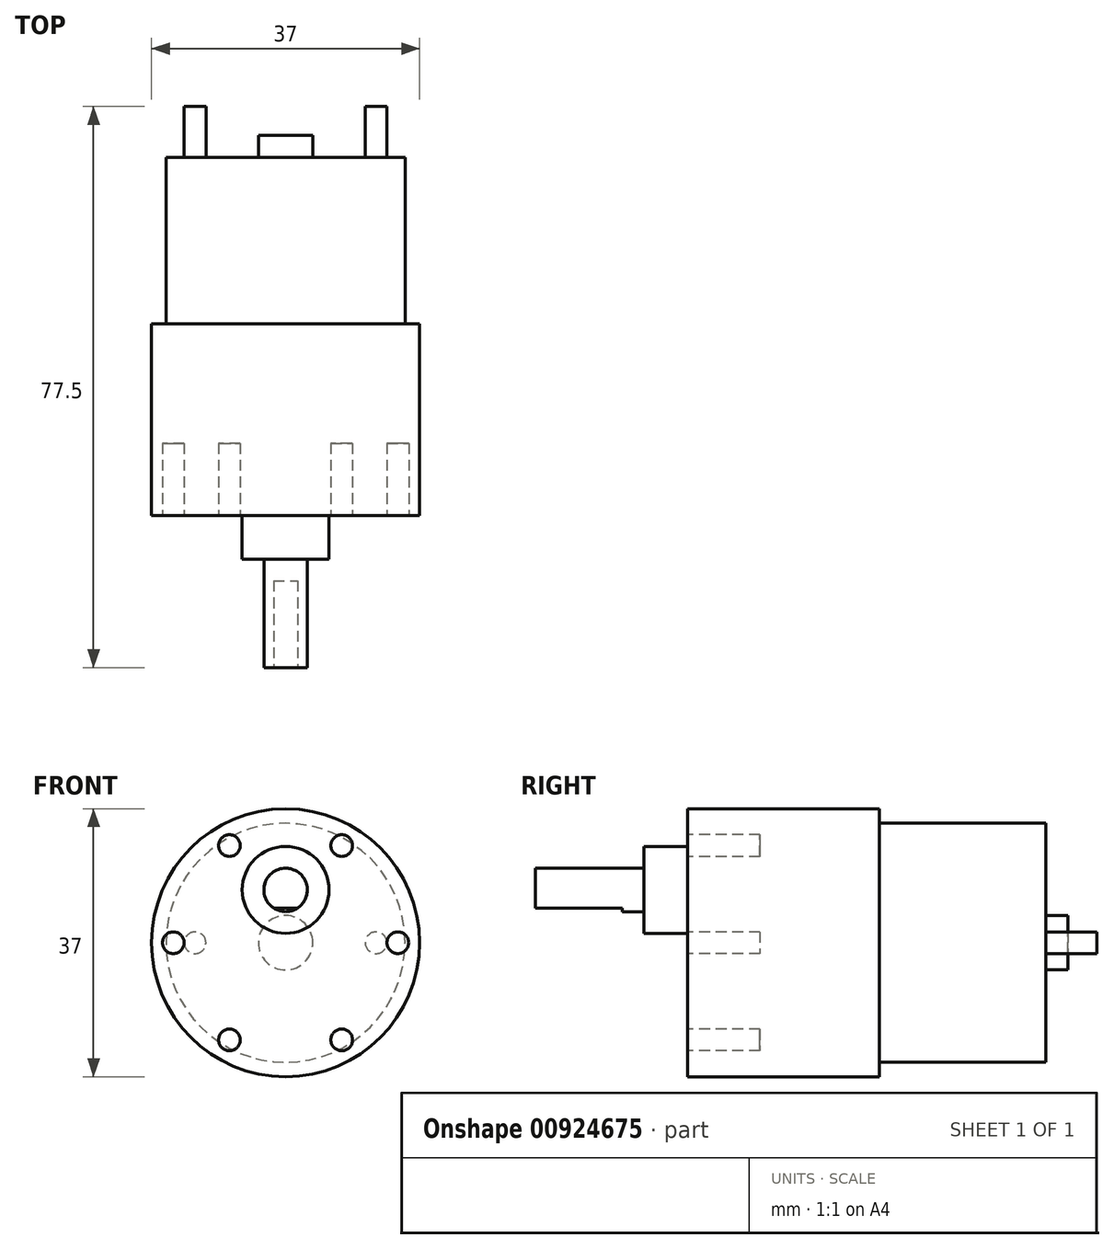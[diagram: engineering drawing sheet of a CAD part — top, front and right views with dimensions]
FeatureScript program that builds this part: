
annotation { "Feature Type Name" : "Feature", "Feature Type Description" : "" }
export const myFeature = defineFeature(function(context is Context, id is Id, definition is map)
    precondition{}
    {
        {
            var Q0;
            Q0=qCreatedBy(makeId("Front.planeOp"),FACE);
            var sketch = newSketch(context, id + "F0", { "sketchPlane" : qUnion([Q0])});
            skCircle(sketch, "E0", {"center": v(0, 0) * mm, "radius": 16.5 * mm});
            skCircle(sketch, "E1", {"center": v(0, 0) * mm, "radius": 18.5 * mm});
            skSolve(sketch);
        }
        {
            var Q0;
            Q0=qSketchRegion(id+"F0",true);
            var Q1;
            Q1=makeQuery(id+"F0.imprint","IMPRINT",FACE,{"disambiguationData":[TD([[makeQuery(id+"F0.imprint","IMPRINT",EDGE,{"derivedFrom":sQuery(id+"F0.wireOp",EDGE,"E0")}),1.0]])]});
            extrude(context, id + "F1", {"entities" : qUnion([Q0, Q1]), "depth" : 26.5 * mm, "offsetDistance" : 25 * mm});
        }
        {
            var Q0;
            Q0=makeQuery(id+"F0.imprint","IMPRINT",FACE,{"disambiguationData":[TD([[makeQuery(id+"F0.imprint","IMPRINT",EDGE,{"derivedFrom":sQuery(id+"F0.wireOp",EDGE,"E0")}),1.0]])]});
            extrude(context, id + "F2", {"entities" : qUnion([Q0]), "operationType" : NewBodyOperationType.ADD, "oppositeDirection" : true, "depth" : 23 * mm, "offsetDistance" : 25 * mm});
        }
        {
            var Q0;
            Q0=makeQuery(id+"F1.opExtrude","CAP_FACE",FACE,{"disambiguationData":[OSD([sQuery(id+"F0.wireOp",EDGE,"E1")])],"isStart":false});
            var sketch = newSketch(context, id + "F3", { "sketchPlane" : qUnion([Q0])});
            skCircle(sketch, "E2", {"center": v(0, 7.3) * mm, "radius": 6 * mm});
            skCircle(sketch, "E3", {"center": v(0, 7.3) * mm, "radius": 3 * mm});
            skPoint(sketch, "E4", {"position": v(0, 1.3) * mm});
            skCircle(sketch, "E5", {"center": v(-15.5, 0) * mm, "radius": 1.5 * mm});
            skSolve(sketch);
        }
        {
            var Q0;
            Q0=makeQuery(id+"F3.imprint","IMPRINT",FACE,{"disambiguationData":[TD([[makeQuery(id+"F3.imprint","IMPRINT",EDGE,{"derivedFrom":sQuery(id+"F3.wireOp",EDGE,"E2")}),1.0]])]});
            extrude(context, id + "F4", {"entities" : qUnion([Q0]), "operationType" : NewBodyOperationType.ADD, "depth" : 6 * mm, "offsetDistance" : 25 * mm});
        }
        {
            var Q0;
            Q0=makeQuery(id+"F4.boolean.opBoolean","SPLIT",FACE,{"disambiguationData":[TD([makeQuery(id+"F4.opExtrude","SWEPT_FACE",FACE,{"disambiguationData":[OSD([sQuery(id+"F3.wireOp",EDGE,"E3")])]})])],"derivedFrom":makeQuery(id+"F1.opExtrude","CAP_FACE",FACE,{"disambiguationData":[OSD([sQuery(id+"F0.wireOp",EDGE,"E1")])],"isStart":false})});
            extrude(context, id + "F5", {"entities" : qUnion([Q0]), "operationType" : NewBodyOperationType.ADD, "depth" : 21 * mm, "offsetDistance" : 25 * mm});
        }
        {
            var Q0;
            Q0=makeQuery(id+"F5.opExtrude","CAP_FACE",FACE,{"disambiguationData":[OSD([sQuery(id+"F0.wireOp",EDGE,"E1")])],"isStart":false});
            var sketch = newSketch(context, id + "F6", { "sketchPlane" : qUnion([Q0])});
            skLineSegment(sketch, "E6", {"start": v(-1.66, 4.8) * mm, "end": v(1.66, 4.8) * mm});
            skArc(sketch, "E7", {"start": v(-1.66, 4.8) * mm, "mid": v(0, 4.3) * mm, "end": v(1.66, 4.8) * mm});
            skSolve(sketch);
        }
        {
            var Q0;
            Q0=makeQuery(id+"F6.imprint","IMPRINT",FACE,{"disambiguationData":[TD([[makeQuery(id+"F6.imprint","IMPRINT",EDGE,{"derivedFrom":sQuery(id+"F6.wireOp",EDGE,"E6")}),-1.0]])]});
            extrude(context, id + "F7", {"entities" : qUnion([Q0]), "operationType" : NewBodyOperationType.REMOVE, "oppositeDirection" : true, "depth" : 12 * mm, "offsetDistance" : 25 * mm});
        }
        {
            var Q0;
            Q0=makeQuery(id+"F3.imprint","IMPRINT",FACE,{"disambiguationData":[TD([[makeQuery(id+"F3.imprint","IMPRINT",EDGE,{"derivedFrom":sQuery(id+"F3.wireOp",EDGE,"E5")}),1.0]])]});
            var Q1;
            Q1=sQuery(id+"F3.wireOp",EDGE,"E5");
            extrude(context, id + "F8", {"entities" : qUnion([Q0]), "surfaceEntities" : qUnion([Q1]), "oppositeDirection" : true, "depth" : 10 * mm, "offsetDistance" : 25 * mm});
        }
        {
            var Q0;
            Q0=qCreatedBy(makeId("Right.planeOp"),FACE);
            var sketch = newSketch(context, id + "F9", { "sketchPlane" : qUnion([Q0])});
            skLineSegment(sketch, "E8", {"start": v(-66.54, 0) * mm, "end": v(54.78, 0) * mm, "construction": true});
            skSolve(sketch);
        }
        {
            var Q0;
            Q0=makeQuery(id+"F8.opExtrude","SWEPT_BODY",BODY,{"disambiguationData":[OSD([sQuery(id+"F3.wireOp",EDGE,"E5")])]});
            var Q1;
            Q1=sQuery(id+"F9.wireOp",EDGE,"E8");
            circularPattern(context, id + "F10", {"operationType" : NewBodyOperationType.REMOVE, "entities" : qUnion([Q0]), "axis" : qUnion([Q1]), "angle" : 360 * degree, "instanceCount" : 6, "equalSpace" : true});
        }
        {
            var Q0;
            Q0=makeQuery(id+"F2.opExtrude","CAP_FACE",FACE,{"disambiguationData":[OSD([sQuery(id+"F0.wireOp",EDGE,"E0")])],"isStart":false});
            var sketch = newSketch(context, id + "F11", { "sketchPlane" : qUnion([Q0])});
            skCircle(sketch, "E9", {"center": v(0, 0) * mm, "radius": 3.75 * mm});
            skCircle(sketch, "E10", {"center": v(-12.5, 0) * mm, "radius": 1.5 * mm});
            skCircle(sketch, "E11", {"center": v(12.5, 0) * mm, "radius": 1.5 * mm});
            skSolve(sketch);
        }
        {
            var Q0;
            Q0=qSketchRegion(id+"F11",true);
            extrude(context, id + "F12", {"entities" : qUnion([Q0]), "operationType" : NewBodyOperationType.ADD, "depth" : 3 * mm, "offsetDistance" : 25 * mm});
        }
        {
            var Q0;
            Q0=makeQuery(id+"F11.imprint","IMPRINT",FACE,{"disambiguationData":[TD([[makeQuery(id+"F11.imprint","IMPRINT",EDGE,{"derivedFrom":sQuery(id+"F11.wireOp",EDGE,"E10")}),1.0]])]});
            var Q1;
            Q1=makeQuery(id+"F11.imprint","IMPRINT",FACE,{"disambiguationData":[TD([[makeQuery(id+"F11.imprint","IMPRINT",EDGE,{"derivedFrom":sQuery(id+"F11.wireOp",EDGE,"E11")}),1.0]])]});
            extrude(context, id + "F13", {"entities" : qUnion([Q0, Q1]), "operationType" : NewBodyOperationType.ADD, "depth" : 7 * mm, "offsetDistance" : 25 * mm});
        }
    });
